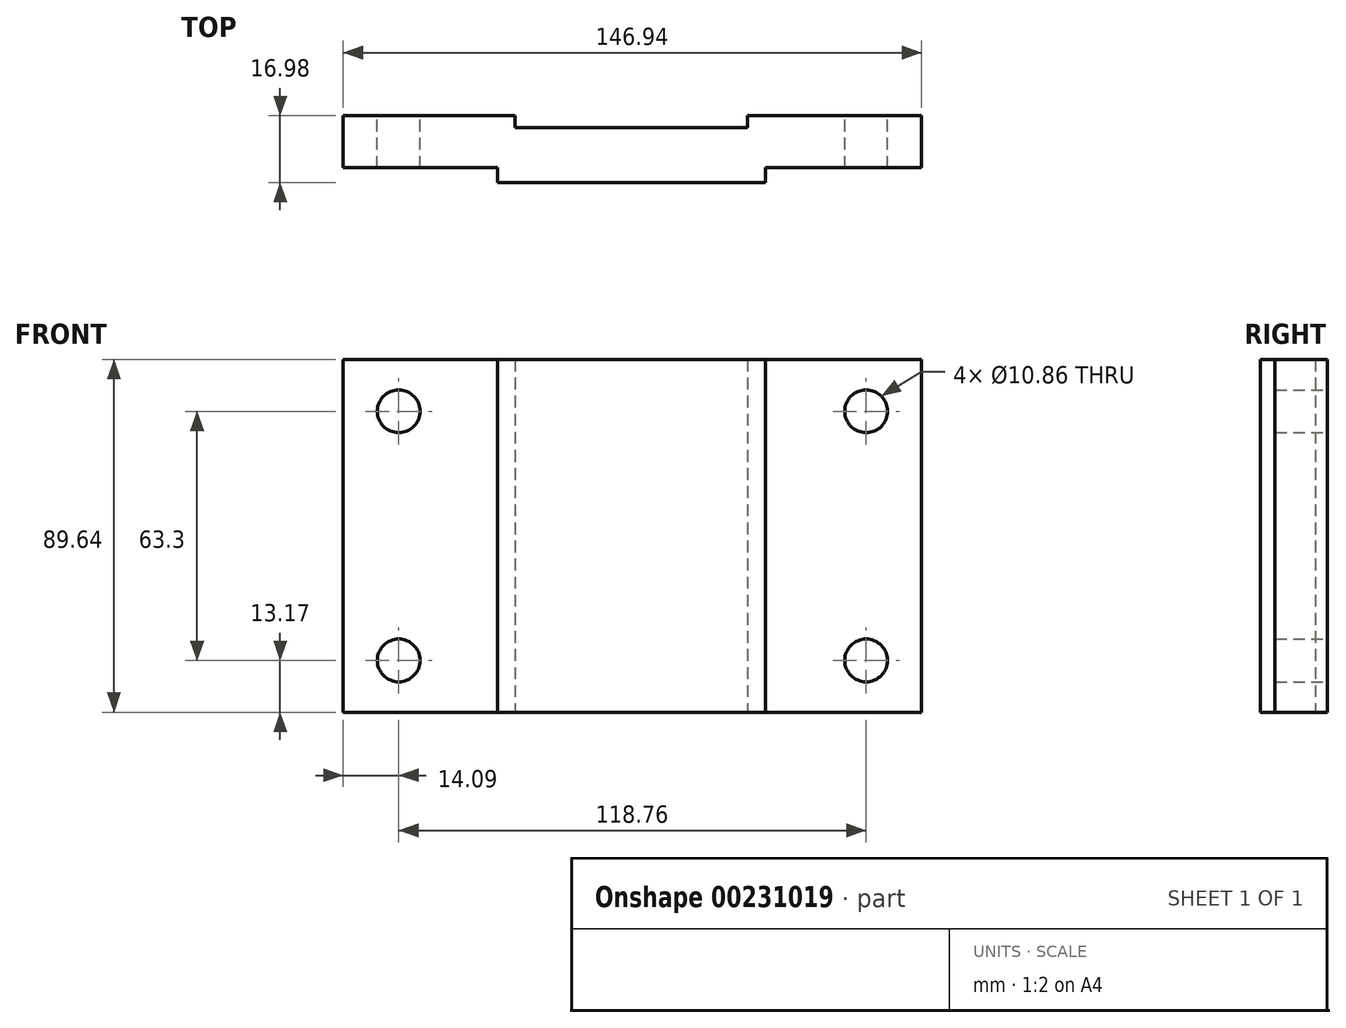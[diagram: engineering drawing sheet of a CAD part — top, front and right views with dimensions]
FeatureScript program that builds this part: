
annotation { "Feature Type Name" : "Feature", "Feature Type Description" : "" }
export const myFeature = defineFeature(function(context is Context, id is Id, definition is map)
    precondition{}
    {
        {
            var Q0;
            Q0=qCreatedBy(makeId("Front.planeOp"),FACE);
            var sketch = newSketch(context, id + "F0", { "sketchPlane" : qUnion([Q0])});
            skLineSegment(sketch, "E0.bottom", {"start": v(73.47, -44.82) * mm, "end": v(-73.47, -44.82) * mm});
            skLineSegment(sketch, "E0.top", {"start": v(73.47, 44.82) * mm, "end": v(-73.47, 44.82) * mm});
            skLineSegment(sketch, "E0.left", {"start": v(73.47, -44.82) * mm, "end": v(73.47, 44.82) * mm});
            skLineSegment(sketch, "E0.right", {"start": v(-73.47, -44.82) * mm, "end": v(-73.47, 44.82) * mm});
            skPoint(sketch, "E0.middle", {"position": v(0, 0) * mm});
            skCircle(sketch, "E1", {"center": v(-59.38, 31.65) * mm, "radius": 5.43 * mm});
            skCircle(sketch, "E2", {"center": v(59.38, 31.65) * mm, "radius": 5.43 * mm});
            skCircle(sketch, "E3", {"center": v(59.38, -31.65) * mm, "radius": 5.43 * mm});
            skCircle(sketch, "E4", {"center": v(-59.38, -31.65) * mm, "radius": 5.43 * mm});
            skLineSegment(sketch, "E5", {"start": v(33.8, 44.82) * mm, "end": v(33.81, -44.82) * mm});
            skLineSegment(sketch, "E6", {"start": v(-34.25, 44.82) * mm, "end": v(-34.25, -44.82) * mm});
            skSolve(sketch);
        }
        {
            var Q0;
            {var subQ0=sQuery(id+"F0.wireOp",EDGE,"E0.left");Q0=makeQuery(id+"F0.imprint","IMPRINT",FACE,{"disambiguationData":[TD([[makeQuery(id+"F0.imprint","IMPRINT",EDGE,{"derivedFrom":subQ0}),1.0]])]});}
            var Q1;
            {var subQ0=sQuery(id+"F0.wireOp",EDGE,"E0.right");Q1=makeQuery(id+"F0.imprint","IMPRINT",FACE,{"disambiguationData":[TD([[makeQuery(id+"F0.imprint","IMPRINT",EDGE,{"derivedFrom":subQ0}),-1.0]])]});}
            extrude(context, id + "F1", {"entities" : qUnion([Q0, Q1]), "depth" : 13.26 * mm});
        }
        {
            var Q0;
            {var subQ0=sQuery(id+"F0.wireOp",EDGE,"E5");Q0=makeQuery(id+"F0.imprint","IMPRINT",FACE,{"disambiguationData":[TD([[makeQuery(id+"F0.imprint","IMPRINT",EDGE,{"derivedFrom":subQ0}),-1.0]])]});}
            extrude(context, id + "F2", {"entities" : qUnion([Q0]), "depth" : 16.98 * mm});
        }
        {
            var Q0;
            Q0=makeQuery(id+"F2.opExtrude","SWEPT_BODY",BODY,{"disambiguationData":[OSD([sQuery(id+"F0.wireOp",EDGE,"E0.bottom"),sQuery(id+"F0.wireOp",EDGE,"E0.top"),sQuery(id+"F0.wireOp",EDGE,"E5"),sQuery(id+"F0.wireOp",EDGE,"E6")])]});
            var Q1;
            Q1=makeQuery(id+"F1.opExtrude","SWEPT_BODY",BODY,{"disambiguationData":[OSD([sQuery(id+"F0.wireOp",EDGE,"E0.bottom"),sQuery(id+"F0.wireOp",EDGE,"E0.top"),sQuery(id+"F0.wireOp",EDGE,"E0.right"),sQuery(id+"F0.wireOp",EDGE,"E1"),sQuery(id+"F0.wireOp",EDGE,"E4"),sQuery(id+"F0.wireOp",EDGE,"E6")])]});
            booleanBodies(context, id + "F3", {"operationType" : BooleanOperationType.UNION, "tools" : qUnion([Q0, Q1])});
        }
        {
            var Q0;
            Q0=makeQuery(id+"F2.opExtrude","SWEPT_BODY",BODY,{"disambiguationData":[OSD([sQuery(id+"F0.wireOp",EDGE,"E0.bottom"),sQuery(id+"F0.wireOp",EDGE,"E0.top"),sQuery(id+"F0.wireOp",EDGE,"E5"),sQuery(id+"F0.wireOp",EDGE,"E6")])]});
            var Q1;
            Q1=makeQuery(id+"F1.opExtrude","SWEPT_BODY",BODY,{"disambiguationData":[OSD([sQuery(id+"F0.wireOp",EDGE,"E0.bottom"),sQuery(id+"F0.wireOp",EDGE,"E0.top"),sQuery(id+"F0.wireOp",EDGE,"E0.left"),sQuery(id+"F0.wireOp",EDGE,"E2"),sQuery(id+"F0.wireOp",EDGE,"E3"),sQuery(id+"F0.wireOp",EDGE,"E5")])]});
            booleanBodies(context, id + "F4", {"operationType" : BooleanOperationType.UNION, "tools" : qUnion([Q0, Q1])});
        }
        {
            var Q0;
            {var subQ0=sQuery(id+"F0.wireOp",EDGE,"E0.bottom");Q0=makeQuery(id+"F4.opBoolean","MERGE",FACE,{"derivedFrom":[makeQuery(id+"F1.opExtrude","SWEPT_FACE",FACE,{"disambiguationData":[OSD([subQ0]),TDD([makeQuery(id+"F0.imprint","IMPRINT",EDGE,{"disambiguationData":[TD([[makeQuery(id+"F0.imprint","INTERSECT",VERTEX,{"derivedFrom":[subQ0,sQuery(id+"F0.wireOp",EDGE,"E0.left")]}),-1.0]])],"derivedFrom":subQ0})])]}),makeQuery(id+"F3.opBoolean","MERGE",FACE,{"derivedFrom":[makeQuery(id+"F1.opExtrude","SWEPT_FACE",FACE,{"disambiguationData":[OSD([subQ0]),TDD([makeQuery(id+"F0.imprint","IMPRINT",EDGE,{"disambiguationData":[TD([[makeQuery(id+"F0.imprint","INTERSECT",VERTEX,{"derivedFrom":[subQ0,sQuery(id+"F0.wireOp",EDGE,"E0.right")]}),1.0]])],"derivedFrom":subQ0})])]}),makeQuery(id+"F2.opExtrude","SWEPT_FACE",FACE,{"disambiguationData":[OSD([subQ0])]})]})]});}
            var sketch = newSketch(context, id + "F5", { "sketchPlane" : qUnion([Q0])});
            skLineSegment(sketch, "E7", {"start": v(73.47, 0) * mm, "end": v(29.2, 0) * mm});
            skLineSegment(sketch, "E8", {"start": v(29.2, 0) * mm, "end": v(29.2, 3.08) * mm});
            skLineSegment(sketch, "E9", {"start": v(29.2, 3.08) * mm, "end": v(-29.77, 3.08) * mm});
            skLineSegment(sketch, "E10", {"start": v(-29.77, 3.08) * mm, "end": v(-29.77, 0) * mm});
            skLineSegment(sketch, "E11", {"start": v(-29.77, 0) * mm, "end": v(-73.47, 0) * mm});
            skLineSegment(sketch, "E12", {"start": v(-73.47, 0) * mm, "end": v(-73.47, -21.7) * mm});
            skLineSegment(sketch, "E13", {"start": v(-73.47, -21.7) * mm, "end": v(73.47, -21.7) * mm});
            skLineSegment(sketch, "E14", {"start": v(73.47, -21.7) * mm, "end": v(73.47, 0) * mm});
            skSolve(sketch);
        }
        {
            var Q0;
            {var subQ1=sQuery(id+"F5.wireOp",EDGE,"E7");Q0=makeQuery(id+"F5.imprint","IMPRINT",FACE,{"disambiguationData":[TD([[makeQuery(id+"F5.imprint","IMPRINT",EDGE,{"derivedFrom":subQ1}),1.0]])]});}
            var Q1;
            {var subQ0=sQuery(id+"F5.wireOp",EDGE,"E8");Q1=makeQuery(id+"F5.imprint","IMPRINT",FACE,{"disambiguationData":[TD([[makeQuery(id+"F5.imprint","IMPRINT",EDGE,{"derivedFrom":subQ0}),1.0]])]});}
            extrude(context, id + "F6", {"entities" : qUnion([Q0, Q1]), "operationType" : NewBodyOperationType.REMOVE, "endBound" : BoundingType.THROUGH_ALL, "oppositeDirection" : true, "depth" : 25 * mm});
        }
    });
